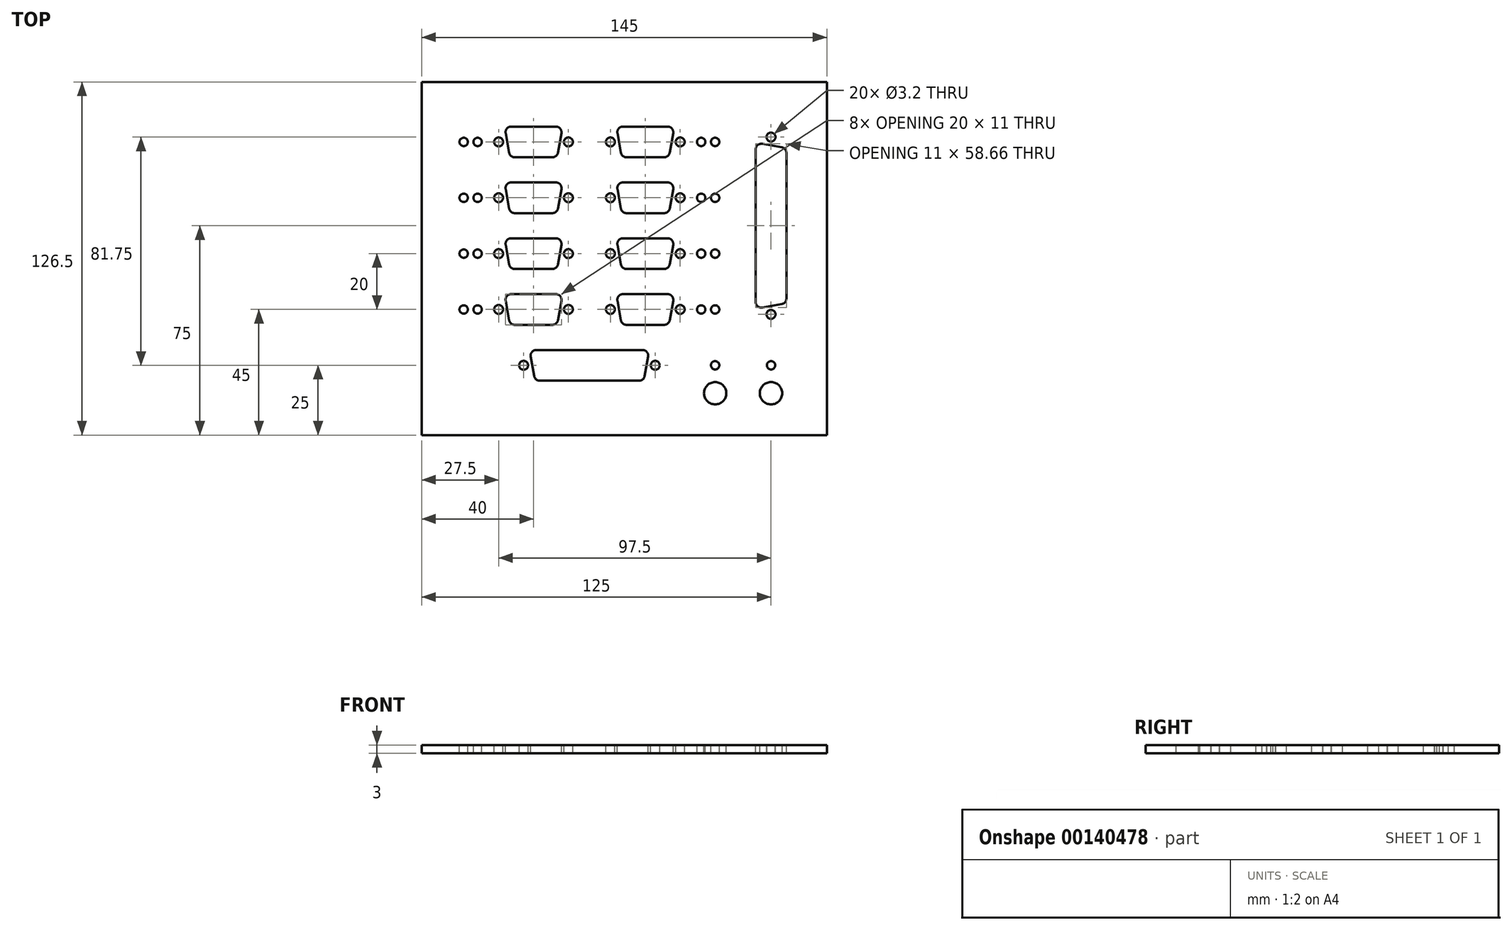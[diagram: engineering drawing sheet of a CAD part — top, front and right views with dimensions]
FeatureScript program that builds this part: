
annotation { "Feature Type Name" : "Feature", "Feature Type Description" : "" }
export const myFeature = defineFeature(function(context is Context, id is Id, definition is map)
    precondition{}
    {
        {
            var Q0;
            Q0=qCreatedBy(makeId("Top.planeOp"),FACE);
            var sketch = newSketch(context, id + "F0", { "sketchPlane" : qUnion([Q0])});
            skLineSegment(sketch, "E0.bottom", {"start": v(0, 0) * mm, "end": v(145, 0) * mm});
            skLineSegment(sketch, "E0.top", {"start": v(0, 126.5) * mm, "end": v(145, 126.5) * mm});
            skLineSegment(sketch, "E0.left", {"start": v(0, 0) * mm, "end": v(0, 126.5) * mm});
            skLineSegment(sketch, "E0.right", {"start": v(145, 0) * mm, "end": v(145, 126.5) * mm});
            skSolve(sketch);
        }
        {
            var Q0;
            Q0 = qSketchRegion(id + "F0", true);
            extrude(context, id + "F1", {"entities" : qUnion([Q0]), "depth" : 3 * mm});
        }
        {
            var Q0;
            Q0=makeQuery(id+"F1.opExtrude","CAP_FACE",FACE,{"disambiguationData":[OSD([sQuery(id+"F0.wireOp",EDGE,"E0.bottom"),sQuery(id+"F0.wireOp",EDGE,"E0.top"),sQuery(id+"F0.wireOp",EDGE,"E0.left"),sQuery(id+"F0.wireOp",EDGE,"E0.right")])],"isStart":false});
            var sketch = newSketch(context, id + "F2", { "sketchPlane" : qUnion([Q0])});
            skCircle(sketch, "E1", {"center": v(15, 105) * mm, "radius": 1.5 * mm});
            skCircle(sketch, "E2", {"center": v(20, 105) * mm, "radius": 1.5 * mm});
            skCircle(sketch, "E3.1.0.0", {"center": v(100, 105) * mm, "radius": 1.5 * mm});
            skCircle(sketch, "E3.1.0.1", {"center": v(105, 105) * mm, "radius": 1.5 * mm});
            skLineSegment(sketch, "E3.direction1", {"start": v(15, 105) * mm, "end": v(100, 105) * mm, "construction": true});
            skCircle(sketch, "E4.0.1.0", {"center": v(15, 85) * mm, "radius": 1.5 * mm});
            skCircle(sketch, "E4.0.1.1", {"center": v(20, 85) * mm, "radius": 1.5 * mm});
            skCircle(sketch, "E4.0.2.0", {"center": v(15, 65) * mm, "radius": 1.5 * mm});
            skCircle(sketch, "E4.0.2.1", {"center": v(20, 65) * mm, "radius": 1.5 * mm});
            skCircle(sketch, "E4.0.3.0", {"center": v(15, 45) * mm, "radius": 1.5 * mm});
            skCircle(sketch, "E4.0.3.1", {"center": v(20, 45) * mm, "radius": 1.5 * mm});
            skLineSegment(sketch, "E4.direction1", {"start": v(15, 105) * mm, "end": v(40, 105) * mm, "construction": true});
            skLineSegment(sketch, "E4.direction2", {"start": v(15, 105) * mm, "end": v(15, 85) * mm, "construction": true});
            skCircle(sketch, "E5.0.1.0", {"center": v(100, 85) * mm, "radius": 1.5 * mm});
            skCircle(sketch, "E5.0.1.1", {"center": v(105, 85) * mm, "radius": 1.5 * mm});
            skCircle(sketch, "E5.0.2.0", {"center": v(100, 65) * mm, "radius": 1.5 * mm});
            skCircle(sketch, "E5.0.2.1", {"center": v(105, 65) * mm, "radius": 1.5 * mm});
            skCircle(sketch, "E5.0.3.0", {"center": v(100, 45) * mm, "radius": 1.5 * mm});
            skCircle(sketch, "E5.0.3.1", {"center": v(105, 45) * mm, "radius": 1.5 * mm});
            skLineSegment(sketch, "E5.direction1", {"start": v(100, 105) * mm, "end": v(125, 105) * mm, "construction": true});
            skLineSegment(sketch, "E5.direction2", {"start": v(100, 105) * mm, "end": v(100, 85) * mm, "construction": true});
            skSolve(sketch);
        }
        {
            var Q0;
            Q0 = qSketchRegion(id + "F2", true);
            extrude(context, id + "F3", {"entities" : qUnion([Q0]), "operationType" : NewBodyOperationType.REMOVE, "endBound" : BoundingType.THROUGH_ALL, "oppositeDirection" : true, "depth" : 25 * mm});
        }
        {
            var Q0;
            Q0=makeQuery(id+"F1.opExtrude","CAP_FACE",FACE,{"disambiguationData":[OSD([sQuery(id+"F0.wireOp",EDGE,"E0.bottom"),sQuery(id+"F0.wireOp",EDGE,"E0.top"),sQuery(id+"F0.wireOp",EDGE,"E0.left"),sQuery(id+"F0.wireOp",EDGE,"E0.right")])],"isStart":false});
            var sketch = newSketch(context, id + "F4", { "sketchPlane" : qUnion([Q0])});
            skCircle(sketch, "E6", {"center": v(27.5, 105) * mm, "radius": 1.6 * mm});
            skCircle(sketch, "E7", {"center": v(67.5, 105) * mm, "radius": 1.6 * mm});
            skCircle(sketch, "E8.0.1.0", {"center": v(27.5, 85) * mm, "radius": 1.6 * mm});
            skCircle(sketch, "E8.0.1.1", {"center": v(67.5, 85) * mm, "radius": 1.6 * mm});
            skCircle(sketch, "E8.0.2.0", {"center": v(27.5, 65) * mm, "radius": 1.6 * mm});
            skCircle(sketch, "E8.0.2.1", {"center": v(67.5, 65) * mm, "radius": 1.6 * mm});
            skCircle(sketch, "E8.0.3.0", {"center": v(27.5, 45) * mm, "radius": 1.6 * mm});
            skCircle(sketch, "E8.0.3.1", {"center": v(67.5, 45) * mm, "radius": 1.6 * mm});
            skCircle(sketch, "E8.1.0.0", {"center": v(52.5, 105) * mm, "radius": 1.6 * mm});
            skCircle(sketch, "E8.1.0.1", {"center": v(92.5, 105) * mm, "radius": 1.6 * mm});
            skCircle(sketch, "E8.1.1.0", {"center": v(52.5, 85) * mm, "radius": 1.6 * mm});
            skCircle(sketch, "E8.1.1.1", {"center": v(92.5, 85) * mm, "radius": 1.6 * mm});
            skCircle(sketch, "E8.1.2.0", {"center": v(52.5, 65) * mm, "radius": 1.6 * mm});
            skCircle(sketch, "E8.1.2.1", {"center": v(92.5, 65) * mm, "radius": 1.6 * mm});
            skCircle(sketch, "E8.1.3.0", {"center": v(52.5, 45) * mm, "radius": 1.6 * mm});
            skCircle(sketch, "E8.1.3.1", {"center": v(92.5, 45) * mm, "radius": 1.6 * mm});
            skLineSegment(sketch, "E8.direction1", {"start": v(27.5, 105) * mm, "end": v(52.5, 105) * mm, "construction": true});
            skLineSegment(sketch, "E8.direction2", {"start": v(27.5, 105) * mm, "end": v(27.5, 85) * mm, "construction": true});
            skSolve(sketch);
        }
        {
            var Q0;
            Q0 = qSketchRegion(id + "F4", true);
            extrude(context, id + "F5", {"entities" : qUnion([Q0]), "operationType" : NewBodyOperationType.REMOVE, "endBound" : BoundingType.THROUGH_ALL, "oppositeDirection" : true, "depth" : 25 * mm});
        }
        {
            var Q0;
            Q0=makeQuery(id+"F1.opExtrude","CAP_FACE",FACE,{"disambiguationData":[OSD([sQuery(id+"F0.wireOp",EDGE,"E0.bottom"),sQuery(id+"F0.wireOp",EDGE,"E0.top"),sQuery(id+"F0.wireOp",EDGE,"E0.left"),sQuery(id+"F0.wireOp",EDGE,"E0.right")])],"isStart":false});
            var sketch = newSketch(context, id + "F6", { "sketchPlane" : qUnion([Q0])});
            skLineSegment(sketch, "E9", {"start": v(32, 110.5) * mm, "end": v(48, 110.5) * mm});
            skLineSegment(sketch, "E10", {"start": v(33.23, 99.5) * mm, "end": v(46.77, 99.5) * mm});
            skLineSegment(sketch, "E11", {"start": v(30.03, 108.15) * mm, "end": v(31.26, 101.15) * mm});
            skLineSegment(sketch, "E12", {"start": v(48.74, 101.15) * mm, "end": v(49.97, 108.15) * mm});
            skPoint(sketch, "E13.visualSharp", {"position": v(29.62, 110.5) * mm});
            skArc(sketch, "E13.filletArc", {"start": v(32, 110.5) * mm, "mid": v(30.47, 109.79) * mm, "end": v(30.03, 108.15) * mm});
            skPoint(sketch, "E14.visualSharp", {"position": v(50.38, 110.5) * mm});
            skArc(sketch, "E14.filletArc", {"start": v(49.97, 108.15) * mm, "mid": v(49.53, 109.79) * mm, "end": v(48, 110.5) * mm});
            skPoint(sketch, "E15.visualSharp", {"position": v(48.44, 99.5) * mm});
            skArc(sketch, "E15.filletArc", {"start": v(46.77, 99.5) * mm, "mid": v(48.05, 99.97) * mm, "end": v(48.74, 101.15) * mm});
            skPoint(sketch, "E16.visualSharp", {"position": v(31.56, 99.5) * mm});
            skArc(sketch, "E16.filletArc", {"start": v(31.26, 101.15) * mm, "mid": v(31.95, 99.97) * mm, "end": v(33.23, 99.5) * mm});
            skLineSegment(sketch, "E17.1.0.0", {"start": v(72, 110.5) * mm, "end": v(88, 110.5) * mm});
            skArc(sketch, "E17.1.0.1", {"start": v(72, 110.5) * mm, "mid": v(70.47, 109.79) * mm, "end": v(70.03, 108.15) * mm});
            skLineSegment(sketch, "E17.1.0.2", {"start": v(70.03, 108.15) * mm, "end": v(71.26, 101.15) * mm});
            skArc(sketch, "E17.1.0.3", {"start": v(71.26, 101.15) * mm, "mid": v(71.95, 99.97) * mm, "end": v(73.23, 99.5) * mm});
            skLineSegment(sketch, "E17.1.0.4", {"start": v(73.23, 99.5) * mm, "end": v(86.77, 99.5) * mm});
            skArc(sketch, "E17.1.0.5", {"start": v(86.77, 99.5) * mm, "mid": v(88.05, 99.97) * mm, "end": v(88.74, 101.15) * mm});
            skLineSegment(sketch, "E17.1.0.6", {"start": v(88.74, 101.15) * mm, "end": v(89.97, 108.15) * mm});
            skArc(sketch, "E17.1.0.7", {"start": v(89.97, 108.15) * mm, "mid": v(89.53, 109.79) * mm, "end": v(88, 110.5) * mm});
            skLineSegment(sketch, "E18.0.1.0", {"start": v(32, 90.5) * mm, "end": v(48, 90.5) * mm});
            skArc(sketch, "E18.0.1.1", {"start": v(32, 90.5) * mm, "mid": v(30.47, 89.79) * mm, "end": v(30.03, 88.15) * mm});
            skLineSegment(sketch, "E18.0.1.2", {"start": v(30.03, 88.15) * mm, "end": v(31.26, 81.15) * mm});
            skLineSegment(sketch, "E18.0.1.3", {"start": v(33.23, 79.5) * mm, "end": v(46.77, 79.5) * mm});
            skArc(sketch, "E18.0.1.4", {"start": v(31.26, 81.15) * mm, "mid": v(31.95, 79.97) * mm, "end": v(33.23, 79.5) * mm});
            skArc(sketch, "E18.0.1.5", {"start": v(46.77, 79.5) * mm, "mid": v(48.05, 79.97) * mm, "end": v(48.74, 81.15) * mm});
            skLineSegment(sketch, "E18.0.1.6", {"start": v(48.74, 81.15) * mm, "end": v(49.97, 88.15) * mm});
            skArc(sketch, "E18.0.1.7", {"start": v(49.97, 88.15) * mm, "mid": v(49.53, 89.79) * mm, "end": v(48, 90.5) * mm});
            skArc(sketch, "E18.0.1.8", {"start": v(72, 90.5) * mm, "mid": v(70.47, 89.79) * mm, "end": v(70.03, 88.15) * mm});
            skLineSegment(sketch, "E18.0.1.9", {"start": v(70.03, 88.15) * mm, "end": v(71.26, 81.15) * mm});
            skLineSegment(sketch, "E18.0.1.10", {"start": v(72, 90.5) * mm, "end": v(88, 90.5) * mm});
            skArc(sketch, "E18.0.1.11", {"start": v(89.97, 88.15) * mm, "mid": v(89.53, 89.79) * mm, "end": v(88, 90.5) * mm});
            skLineSegment(sketch, "E18.0.1.12", {"start": v(88.74, 81.15) * mm, "end": v(89.97, 88.15) * mm});
            skArc(sketch, "E18.0.1.13", {"start": v(86.77, 79.5) * mm, "mid": v(88.05, 79.97) * mm, "end": v(88.74, 81.15) * mm});
            skLineSegment(sketch, "E18.0.1.14", {"start": v(73.23, 79.5) * mm, "end": v(86.77, 79.5) * mm});
            skArc(sketch, "E18.0.1.15", {"start": v(71.26, 81.15) * mm, "mid": v(71.95, 79.97) * mm, "end": v(73.23, 79.5) * mm});
            skLineSegment(sketch, "E18.0.2.0", {"start": v(32, 70.5) * mm, "end": v(48, 70.5) * mm});
            skArc(sketch, "E18.0.2.1", {"start": v(32, 70.5) * mm, "mid": v(30.47, 69.79) * mm, "end": v(30.03, 68.15) * mm});
            skLineSegment(sketch, "E18.0.2.2", {"start": v(30.03, 68.15) * mm, "end": v(31.26, 61.15) * mm});
            skLineSegment(sketch, "E18.0.2.3", {"start": v(33.23, 59.5) * mm, "end": v(46.77, 59.5) * mm});
            skArc(sketch, "E18.0.2.4", {"start": v(31.26, 61.15) * mm, "mid": v(31.95, 59.97) * mm, "end": v(33.23, 59.5) * mm});
            skArc(sketch, "E18.0.2.5", {"start": v(46.77, 59.5) * mm, "mid": v(48.05, 59.97) * mm, "end": v(48.74, 61.15) * mm});
            skLineSegment(sketch, "E18.0.2.6", {"start": v(48.74, 61.15) * mm, "end": v(49.97, 68.15) * mm});
            skArc(sketch, "E18.0.2.7", {"start": v(49.97, 68.15) * mm, "mid": v(49.53, 69.79) * mm, "end": v(48, 70.5) * mm});
            skArc(sketch, "E18.0.2.8", {"start": v(72, 70.5) * mm, "mid": v(70.47, 69.79) * mm, "end": v(70.03, 68.15) * mm});
            skLineSegment(sketch, "E18.0.2.9", {"start": v(70.03, 68.15) * mm, "end": v(71.26, 61.15) * mm});
            skLineSegment(sketch, "E18.0.2.10", {"start": v(72, 70.5) * mm, "end": v(88, 70.5) * mm});
            skArc(sketch, "E18.0.2.11", {"start": v(89.97, 68.15) * mm, "mid": v(89.53, 69.79) * mm, "end": v(88, 70.5) * mm});
            skLineSegment(sketch, "E18.0.2.12", {"start": v(88.74, 61.15) * mm, "end": v(89.97, 68.15) * mm});
            skArc(sketch, "E18.0.2.13", {"start": v(86.77, 59.5) * mm, "mid": v(88.05, 59.97) * mm, "end": v(88.74, 61.15) * mm});
            skLineSegment(sketch, "E18.0.2.14", {"start": v(73.23, 59.5) * mm, "end": v(86.77, 59.5) * mm});
            skArc(sketch, "E18.0.2.15", {"start": v(71.26, 61.15) * mm, "mid": v(71.95, 59.97) * mm, "end": v(73.23, 59.5) * mm});
            skLineSegment(sketch, "E18.0.3.0", {"start": v(32, 50.5) * mm, "end": v(48, 50.5) * mm});
            skArc(sketch, "E18.0.3.1", {"start": v(32, 50.5) * mm, "mid": v(30.47, 49.79) * mm, "end": v(30.03, 48.15) * mm});
            skLineSegment(sketch, "E18.0.3.2", {"start": v(30.03, 48.15) * mm, "end": v(31.26, 41.15) * mm});
            skLineSegment(sketch, "E18.0.3.3", {"start": v(33.23, 39.5) * mm, "end": v(46.77, 39.5) * mm});
            skArc(sketch, "E18.0.3.4", {"start": v(31.26, 41.15) * mm, "mid": v(31.95, 39.97) * mm, "end": v(33.23, 39.5) * mm});
            skArc(sketch, "E18.0.3.5", {"start": v(46.77, 39.5) * mm, "mid": v(48.05, 39.97) * mm, "end": v(48.74, 41.15) * mm});
            skLineSegment(sketch, "E18.0.3.6", {"start": v(48.74, 41.15) * mm, "end": v(49.97, 48.15) * mm});
            skArc(sketch, "E18.0.3.7", {"start": v(49.97, 48.15) * mm, "mid": v(49.53, 49.79) * mm, "end": v(48, 50.5) * mm});
            skArc(sketch, "E18.0.3.8", {"start": v(72, 50.5) * mm, "mid": v(70.47, 49.79) * mm, "end": v(70.03, 48.15) * mm});
            skLineSegment(sketch, "E18.0.3.9", {"start": v(70.03, 48.15) * mm, "end": v(71.26, 41.15) * mm});
            skLineSegment(sketch, "E18.0.3.10", {"start": v(72, 50.5) * mm, "end": v(88, 50.5) * mm});
            skArc(sketch, "E18.0.3.11", {"start": v(89.97, 48.15) * mm, "mid": v(89.53, 49.79) * mm, "end": v(88, 50.5) * mm});
            skLineSegment(sketch, "E18.0.3.12", {"start": v(88.74, 41.15) * mm, "end": v(89.97, 48.15) * mm});
            skArc(sketch, "E18.0.3.13", {"start": v(86.77, 39.5) * mm, "mid": v(88.05, 39.97) * mm, "end": v(88.74, 41.15) * mm});
            skLineSegment(sketch, "E18.0.3.14", {"start": v(73.23, 39.5) * mm, "end": v(86.77, 39.5) * mm});
            skArc(sketch, "E18.0.3.15", {"start": v(71.26, 41.15) * mm, "mid": v(71.95, 39.97) * mm, "end": v(73.23, 39.5) * mm});
            skSolve(sketch);
        }
        {
            var Q0;
            Q0=makeQuery(id+"F6.imprint","IMPRINT",FACE,{"disambiguationData":[TD([[makeQuery(id+"F6.imprint","IMPRINT",EDGE,{"derivedFrom":sQuery(id+"F6.wireOp",EDGE,"E9")}),1.0]])]});
            var sketch = newSketch(context, id + "F7", { "sketchPlane" : qUnion([Q0])});
            skCircle(sketch, "E19", {"center": v(125, 106.75) * mm, "radius": 1.6 * mm});
            skCircle(sketch, "E20", {"center": v(125, 43.25) * mm, "radius": 1.6 * mm});
            skSolve(sketch);
        }
        {
            var Q0;
            Q0 = qSketchRegion(id + "F7", true);
            extrude(context, id + "F8", {"entities" : qUnion([Q0]), "operationType" : NewBodyOperationType.REMOVE, "endBound" : BoundingType.THROUGH_ALL, "oppositeDirection" : true, "depth" : 25 * mm});
        }
        {
            var Q0;
            Q0=makeQuery(id+"F6.imprint","IMPRINT",FACE,{"disambiguationData":[TD([[makeQuery(id+"F6.imprint","IMPRINT",EDGE,{"derivedFrom":sQuery(id+"F6.wireOp",EDGE,"E9")}),1.0]])]});
            var sketch = newSketch(context, id + "F9", { "sketchPlane" : qUnion([Q0])});
            skCircle(sketch, "E21", {"center": v(36.45, 25) * mm, "radius": 1.6 * mm});
            skCircle(sketch, "E22", {"center": v(83.55, 25) * mm, "radius": 1.6 * mm});
            skSolve(sketch);
        }
        {
            var Q0;
            Q0 = qSketchRegion(id + "F9", true);
            extrude(context, id + "F10", {"entities" : qUnion([Q0]), "operationType" : NewBodyOperationType.REMOVE, "endBound" : BoundingType.THROUGH_ALL, "oppositeDirection" : true, "depth" : 25 * mm});
        }
        {
            var Q0;
            Q0=makeQuery(id+"F6.imprint","IMPRINT",FACE,{"disambiguationData":[TD([[makeQuery(id+"F6.imprint","IMPRINT",EDGE,{"derivedFrom":sQuery(id+"F6.wireOp",EDGE,"E9")}),1.0]])]});
            var sketch = newSketch(context, id + "F11", { "sketchPlane" : qUnion([Q0])});
            skCircle(sketch, "E23", {"center": v(105, 15) * mm, "radius": 4 * mm});
            skCircle(sketch, "E24", {"center": v(125, 15) * mm, "radius": 4 * mm});
            skCircle(sketch, "E25", {"center": v(105, 25) * mm, "radius": 1.5 * mm});
            skCircle(sketch, "E26", {"center": v(125, 25) * mm, "radius": 1.5 * mm});
            skSolve(sketch);
        }
        {
            var Q0;
            Q0 = qSketchRegion(id + "F11", true);
            extrude(context, id + "F12", {"entities" : qUnion([Q0]), "operationType" : NewBodyOperationType.REMOVE, "endBound" : BoundingType.THROUGH_ALL, "oppositeDirection" : true, "depth" : 25 * mm});
        }
        {
            var Q0;
            Q0 = qSketchRegion(id + "F6", true);
            extrude(context, id + "F13", {"entities" : qUnion([Q0]), "operationType" : NewBodyOperationType.REMOVE, "endBound" : BoundingType.THROUGH_ALL, "oppositeDirection" : true, "depth" : 25 * mm});
        }
        {
            var Q0;
            Q0=makeQuery(id+"F1.opExtrude","CAP_FACE",FACE,{"disambiguationData":[OSD([sQuery(id+"F0.wireOp",EDGE,"E0.bottom"),sQuery(id+"F0.wireOp",EDGE,"E0.top"),sQuery(id+"F0.wireOp",EDGE,"E0.left"),sQuery(id+"F0.wireOp",EDGE,"E0.right")])],"isStart":false});
            var sketch = newSketch(context, id + "F14", { "sketchPlane" : qUnion([Q0])});
            skLineSegment(sketch, "E27", {"start": v(119.5, 102.33) * mm, "end": v(119.5, 47.67) * mm});
            skLineSegment(sketch, "E28", {"start": v(130.5, 101.1) * mm, "end": v(130.5, 48.9) * mm});
            skLineSegment(sketch, "E29", {"start": v(121.85, 104.3) * mm, "end": v(128.85, 103.07) * mm});
            skLineSegment(sketch, "E30", {"start": v(128.85, 46.93) * mm, "end": v(121.85, 45.7) * mm});
            skPoint(sketch, "E31.visualSharp", {"position": v(119.5, 104.71) * mm});
            skArc(sketch, "E31.filletArc", {"start": v(121.85, 104.3) * mm, "mid": v(120.21, 103.86) * mm, "end": v(119.5, 102.33) * mm});
            skPoint(sketch, "E32.visualSharp", {"position": v(130.5, 102.77) * mm});
            skArc(sketch, "E32.filletArc", {"start": v(130.5, 101.1) * mm, "mid": v(130.03, 102.38) * mm, "end": v(128.85, 103.07) * mm});
            skPoint(sketch, "E33.visualSharp", {"position": v(130.5, 47.23) * mm});
            skArc(sketch, "E33.filletArc", {"start": v(128.85, 46.93) * mm, "mid": v(130.03, 47.62) * mm, "end": v(130.5, 48.9) * mm});
            skPoint(sketch, "E34.visualSharp", {"position": v(119.5, 45.29) * mm});
            skArc(sketch, "E34.filletArc", {"start": v(119.5, 47.67) * mm, "mid": v(120.21, 46.14) * mm, "end": v(121.85, 45.7) * mm});
            skSolve(sketch);
        }
        {
            var Q0;
            Q0 = qSketchRegion(id + "F14", true);
            extrude(context, id + "F15", {"entities" : qUnion([Q0]), "operationType" : NewBodyOperationType.REMOVE, "endBound" : BoundingType.THROUGH_ALL, "oppositeDirection" : true, "depth" : 25 * mm});
        }
        {
            var Q0;
            Q0=makeQuery(id+"F1.opExtrude","CAP_FACE",FACE,{"disambiguationData":[OSD([sQuery(id+"F0.wireOp",EDGE,"E0.bottom"),sQuery(id+"F0.wireOp",EDGE,"E0.top"),sQuery(id+"F0.wireOp",EDGE,"E0.left"),sQuery(id+"F0.wireOp",EDGE,"E0.right")])],"isStart":false});
            var sketch = newSketch(context, id + "F16", { "sketchPlane" : qUnion([Q0])});
            skLineSegment(sketch, "E35", {"start": v(40.97, 30.5) * mm, "end": v(79.03, 30.5) * mm});
            skLineSegment(sketch, "E36", {"start": v(81, 28.15) * mm, "end": v(79.77, 21.15) * mm});
            skLineSegment(sketch, "E37", {"start": v(77.8, 19.5) * mm, "end": v(42.2, 19.5) * mm});
            skLineSegment(sketch, "E38", {"start": v(40.23, 21.15) * mm, "end": v(39, 28.15) * mm});
            skPoint(sketch, "E39.visualSharp", {"position": v(38.59, 30.5) * mm});
            skArc(sketch, "E39.filletArc", {"start": v(40.97, 30.5) * mm, "mid": v(39.44, 29.79) * mm, "end": v(39, 28.15) * mm});
            skPoint(sketch, "E40.visualSharp", {"position": v(81.41, 30.5) * mm});
            skArc(sketch, "E40.filletArc", {"start": v(81, 28.15) * mm, "mid": v(80.56, 29.79) * mm, "end": v(79.03, 30.5) * mm});
            skPoint(sketch, "E41.visualSharp", {"position": v(79.47, 19.5) * mm});
            skArc(sketch, "E41.filletArc", {"start": v(77.8, 19.5) * mm, "mid": v(79.08, 19.97) * mm, "end": v(79.77, 21.15) * mm});
            skPoint(sketch, "E42.visualSharp", {"position": v(40.53, 19.5) * mm});
            skArc(sketch, "E42.filletArc", {"start": v(40.23, 21.15) * mm, "mid": v(40.92, 19.97) * mm, "end": v(42.2, 19.5) * mm});
            skSolve(sketch);
        }
        {
            var Q0;
            Q0 = qSketchRegion(id + "F16", true);
            extrude(context, id + "F17", {"entities" : qUnion([Q0]), "operationType" : NewBodyOperationType.REMOVE, "endBound" : BoundingType.THROUGH_ALL, "oppositeDirection" : true, "depth" : 25 * mm});
        }
    });
